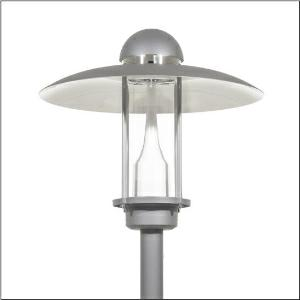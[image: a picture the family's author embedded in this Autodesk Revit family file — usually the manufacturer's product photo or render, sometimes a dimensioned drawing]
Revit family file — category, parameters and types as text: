
# Revit family: city-light_elegance_iq___st1_2a_5xa5265kf14h_1fe5
name_source: partatom
category: Lighting Fixtures
units: mm (PartAtom-declared; Revit-internal decimal feet)

## family parameters
Cut with Voids When Loaded = No
Host = Face
Light Source = No
Part Type = Normal
Room Calculation Point = No
Round Connector Dimension = Use Diameter
Shared = No

## types (1)
- --- (1 x LED, 1470 lm, 10 W, 4000K)
    Apparent Load = 10 VA
    CIE Flux Codes = 22 62 94 98 100
    Color Rendering = 70
    Color Temperature = 4000K
    Default Elevation = 1800 mm
    Description = City-Light Elegance iQ, mast luminaire, Module 540 iQ-SR, primary light control with 3 zone facetted reflector, of plastic, silver coated, highly specular, structured, primary optical cover: cover, of PMMA, transparent, light distribution: ST1.2a, light emission: direct distribution, primary light characteristic: asymmetric, installation type: post-top, LED, High Power LED, rated luminous flux: 1.470lm, luminous efficacy: 147lm/W, light colour: 740, colour temperature: 4000K, control gear: ECG iQ, control: pre-setting: logarithmic dimming characteristic, Street-Remote, Auto-Match, Temp-Guard, Lumen-Switch, Night-Set, Smart-Wire, Light-Fading, Desk-Remote (wireless, voltage-free reading and setting of iQ features in the workshop via application-optimized NFC function/RFID function), optimised constant luminous flux control (CLO 2.0), with terminal, 6-pole, max. 2.5mm², mains connection: 230..240V, AC, 50/60Hz, start of lifetime: 10W, end of service life: 10W, reduction: 5W, luminaire housing, upper part, of aluminium, coated, Siteco® metallic grey (DB 702S), diameter: 750mm, height: 675mm, spigot size: d x l = 76 x 70mm (post-top) | with reducer (optional accessory) 60 x 70mm, post-top mast mounting element, of diecast aluminium, coated, Siteco® metallic grey (DB 702S), Module 540 iQ-SR, traffic white (RAL 9016), equipment: standard, protection rating (complete): IP65, insulation class (complete): insulation class II (safety insulation), certification: CE, ENEC, VDE, packaging unit: 1 piece

Light Distribution: ST1.2a
    Height = 675 mm
    Lamp = 1 x LED
    Lamp Light Flux = 1470 lm
    Lamp Power = 10 W
    Lamp count = 1
    Length = 750 mm
    Luminous efficacy = 147 lm/W
    Manufacturer = Siteco
    ModVariant = No
    Model = 5XA5265KF14H
    Number of Poles = 1
    OnlyDefault = Yes
    Power Factor = 1
    Product Name = City-Light Elegance iQ | ST1.2a
    Product group = mast luminaire | pylon top
    ProductGroupID = 6100
    Protection Class = Protection class II
    Protection Degree = IP 65
    RLX_Detail_Level = 1
    RLX_Emergency_Light_Flux = 0 lm
    RLX_Emergency_Type = 0
    RLX_Emergency_Type_DB = No
    RlxData = <blob elided: 103909 chars, md5=dc6a7f44>
    Socket = socket
    Standby Power = 0 W
    System Light Flux = 1470 lm
    System Power = 10 W
    Type Comments = factory setting: luminous flux: 100 % | dim-lin: 254 | 401 mA
    Type Image = l_1006912.jpg
    URL = http://relux.com
    VarID = @adj_130181
    Voltage = 0 V
    Weight = 0.00 kg
    Width = 0 mm  [stored 0 ft]

note: [stored X ft] marks values corroborated as IEEE doubles in the binary element streams (Revit-internal decimal feet)

## geometry (parser evidence)
native form markers: Blend x4, Sweep x12
no freeform markers — native parametric forms only
